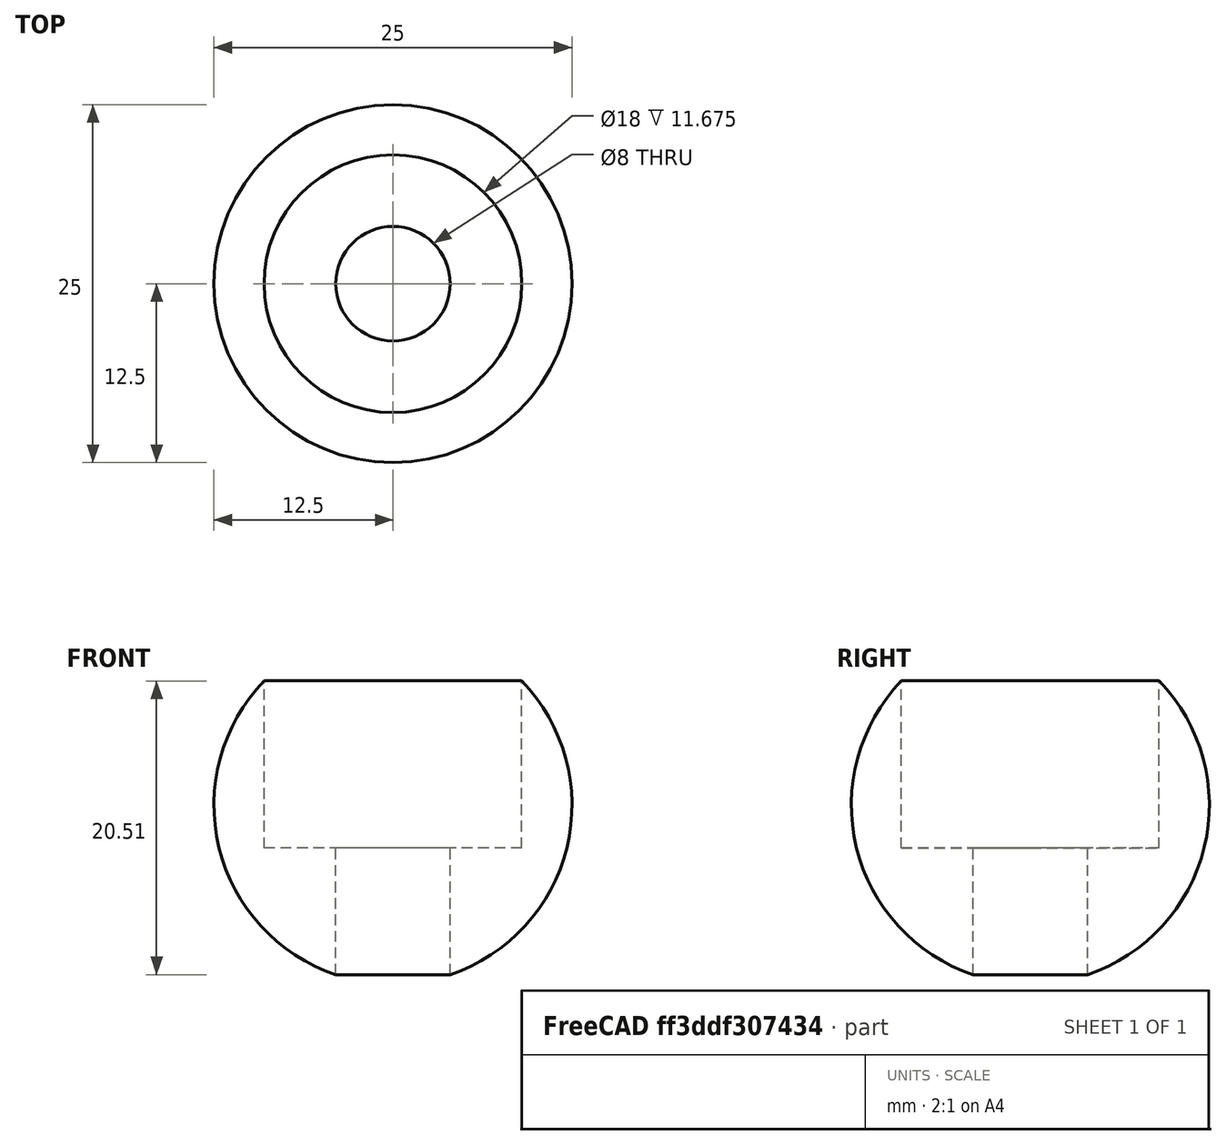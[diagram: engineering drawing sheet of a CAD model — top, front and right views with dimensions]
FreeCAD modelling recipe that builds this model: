
FCSTD DOCUMENT  (FreeCAD 0.18R4 (GitTag))
Label: Rubber Ball
License: All rights reserved
LicenseURL: http://en.wikipedia.org/wiki/All_rights_reserved
objects: Part::Cylinder×2, Part::Sphere×1, Part::MultiFuse×1, Part::Cut×1
note: 5 computed .brp shape members not serialized (recipe doc carries the construction recipe); baked Part::Feature solids carry a one-line shape summary decoded from their .brp

FEATURE [Part::Sphere] Sphere
  Angle1 = -90
  Angle2 = 90
  Angle3 = 360
  AttacherType = Attacher::AttachEngine3D
  Radius = 12.5
FEATURE [Part::Cylinder] Cylinder
  Angle = 360
  AttacherType = Attacher::AttachEngine3D
  Height = 30
  Placement = pos=(0,0,-15) rot=(0,0,1;0rad)
  Radius = 4
FEATURE [Part::Cylinder] Cylinder001
  Angle = 360
  AttacherType = Attacher::AttachEngine3D
  Height = 15
  Placement = pos=(0,0,-3) rot=(0,0,1;0rad)
  Radius = 9
FEATURE [Part::MultiFuse] Fusion
  Refine = true
  Shapes = -> [Cylinder,Cylinder001]
FEATURE [Part::Cut] Cut  label="Final"
  Base = -> Sphere
  Refine = true
  Tool = -> Fusion
